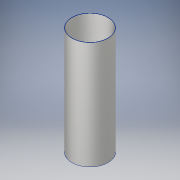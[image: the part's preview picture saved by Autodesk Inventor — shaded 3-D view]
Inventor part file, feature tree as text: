
AUTODESK INVENTOR PART (.ipt)
format: ipt  version: 2017 SP1 (Build 210196100, 196)  size: 99,328 bytes
history: native  units: in
note: dims shown in document units (in); Inventor stores cm internally (conversion verified against a paired STEP export)
features: extrude x1, sketch x1
ambient origin geometry x8: Origin, YZ Plane, XZ Plane, XY Plane, X Axis, Y Axis, Z Axis, Center Point
bodies: Solid1 (feature_tree)
feature tree (2):
  extrude  "Extrusion1"  Depth=24.17in
  sketch  "Sketch1"  dims[d0=8.125in d1=8.0in d2=24.17in d3=0.0in]
